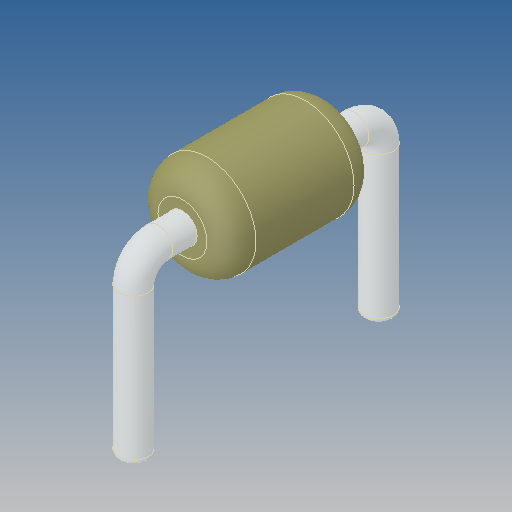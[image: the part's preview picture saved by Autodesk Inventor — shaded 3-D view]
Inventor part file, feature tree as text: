
AUTODESK INVENTOR PART (.ipt)
format: ipt  version: 2020 (Build 240168000, 168)  size: 154,112 bytes
history: mixed  units: mm
features: other x1, fillet x1, imported_body x1
ambient origin geometry x8: Origin, YZ Plane, XZ Plane, XY Plane, X Axis, Y Axis, Z Axis, Center Point
bodies: Body1 (imported_parasolid)
feature tree (3):
  other  "Твердое тело1"
  fillet  "Fillet2"  [1 undecoded]
  imported_body  NMx_Import_Brep_tag  [imported B-rep: ~15 faces, bbox_mm=[1.0, 3.8, 5.6]]
note: 1 required parameter value undecoded (feature->parameter linkage not recoverable at this tier; creation-order binding heuristic only, values carry confidence <= 0.55)
